# Revit family: 1. Sálvora_PDroite_FRA
name_source: partatom
category: Modelos genéricos
revit_build: Autodesk Revit LT 2017 (Build: 20160225_1515(x64)
units: mm (PartAtom-declared; Revit-internal decimal feet)

## family parameters
Anfitrión = Muro
Compartido = No
Corte con vacíos al cargar = No
Cota de conector redondo = Diámetro de uso
Puede alojar armadura = No
Punto de cálculo de habitación = No
Siempre vertical = Sí
Tipo de pieza = Normal

## types (1)
- Stonepanel®Sálvora
    Absorption = Basse absorption
    Advantages de Stonepanel = Efficacité:  L’installation des panneaux est simple et facile. Elle n’implique pas l’utilisation de machines spécifiques. La pose est dix fois plus rapide que la pose traditionnelle (20 m2 en moyenne par jour). La longévité de ce produit naturel est supérieure aux autres types de revêtement. Les déchets et les pertes dues aux coupes sont amplement diminués durant le chantier.
Sécurité: Le système de fixation breveté et homologué, en acier inoxydable, permet l’installation à plus de 2 mètres de hauteur (Avis Technique, CSTB). La base en ciment, homogène et rugueuse, garantit l’adhésion et permet d’être coupée sans décollement des pierres.
Qualité: Le contrôle de la production est effectué de façon continue par le département Innovation de CUPAGROUP. Chaque pierre naturelle est sélectionnée avec une attention particulière par les experts de CUPA STONE. Angles courts, longs, massifs, doubles, pour les fenêtres ou les dessus de mur… De nombreuses pièces spéciales sont proposées en option pour s’adapter parfaitement aux différentes configurations de chantier.
Esthétisme: Le parement en forme de « S » rend les joints invisibles et assure un aspect homogène à la surface installée. Notre gamme de parements en pierre naturelle permet de choisir parmi un large choix de finitions et de coloris. Chaque pierre est unique, ainsi chaque panneau révèle l’élégance et la noblesse de la pierre naturelle.
    Apparence = Rustique
    Autres données intéressants = STONEPANEL SKY  est utilisé pour la réalisation de revêtements de murs intérieurs ou extérieurs, pour des ouvrages de 12 m de haut au plus.
    Certificats = Avis Technique - France - En cours
    Couleur principale = Marron
    Couleur secondaire = Gris rougeâtre
    Densité apparente = 86,5 kg/m2
    Descripción = Système de panneaux de pierre naturelle prémontés et assemblés
sur une base en ciment renforcée, sur la face arrière, par une armature en fibre de verre. 
Son système de fixation unique évite tout risque de décollement. Est un ancrage spécifique pour les installations
à plus de 2 mètres de hauteur.
    Durabilité = La durabilité de l’ouvrage peut être appréciée comme équivalente à celle d’un carrelage collé en façade.
    Décalage de hauteur = 0 mm  [stored 0 ft]
    Détails de construction = Détails de:
- Mise en oeuvre avec un profilé en métal
- Mise en oeuvre de Stonepanel
- Mise en oeuvre de Stonepanel en murs intérieurs
- Mise en oeuvre de l'élément de sécurité
- Angles rentrants
- Angles sortants avec continuité de Stonepanel - éléments d'angles
- Angles sortants avec continuité de Stonepanel - angles préformés
- Angles sortants avec continuité de Stonepanel - sciage d'un panneau
- Angles sortants sans continuité de Stonepanel - cas d'un pignon isolé
- Arêtes supérieures
- Dessus d'acrotère
- Encadrement de baie
    Fabricante = Cupastone
    Finiton = Naturelle
    Form = Forme de « S »
    Format = 600 x 200
    Haut = 200 mm  [stored 0.656168 ft]
    Imagen de tipo = <Ninguno>
    Largeur = 50 mm  [stored 0.164042 ft]
    Long = 600 mm
    Matérial = Ardoise marron rougeâtre dont les nuances varient du clair au plus foncé pour doter les intérieurs contemporains d’une ambiance originale.
    Modelo = Stonepanel® Sálvora
    NBS Reference = 45-25-45/380 Natural stone panels
    Nettoyage = En général, les panneaux ne nécessitent pas d'entretien et sont autonettoyants, mais la suppression de certains types de marques peuvent nécessiter un traitement spécialisé.
Pour les salissures anormales, la surface peut être nettoyée à l'aide d'un mélange eau / détergent chaud, appliqué avec un tampon de nettoyage approprié ou une éponge.
    Omniclass = 23-15 15 15 11
    Oxydation = Non oxidé
    Poids = 9,5 kg
    Résistance = Résistance élevée
    Résistance au feu = STONEPANEL ne sont pas de nature à affecter la tenue au feu des ouvrages.
    Système d'ancrage = Bande perforée en acier inoxydable:
- Nature de l’acier : AISI 316 (1.4401) ou AISI 304 (1.4301)
- Epaisseur minimale (mm) : 0,7
- Largeur (mm) : 12 à 15
- Diamètre du trou (mm) : 6 ± 1

Chevilles:
Le choix des chevilles de fixation doit être déterminé compte tenu de l’action en dépression du vent (murs extérieurs) et de la résistance des chevilles dans le support considéré en fonction de de la nature du support. Un exemple de cheville à utiliser est TAPCO TC 6/30 x 60.
La charge admissible des chevilles est égale à 1/K fois la résistance caractéristique indiquée dans l’Agrément Technique Européen de la cheville ou :
   K = 1,75 par comparaison au vent normal
   K = 3 par comparaison au vent extrême
Les chevilles doivent être adaptées à la nature du support porteur.
    Tests effectués par Avis Technique = Avis Technique
Résistance mécanique de l'ancrage
Résistance mécanique de l'attache de sécurité
Essais de durabilité après action de l'eau
Essais de durabilité après action du gel
Essai sismique
Essai vers le feu
Résistance mécanique de l'attache de sécurité
Essais de durabilité après action de l'eau
Essais de durabilité après action du gel
Essai sismique
    Type de livraison = Les panneaux sont emballés en plastique, en paires.
    URL = http://www.cupastone.fr
    Uniclass 2 = Pr_25_71_14_56 Natural stone panels
    Uniclass 2015 = Pr_25_71_14_56 Natural stone panels
    Utilisations indiquées = Revêtements de murs intérieurs ou extérieurs, pour des ouvrages de 12 m de haut au plus.
En murs intérieurs, les supports admis sont les suivants (ils doivent avoir une épaisseur de 6 cm minimum) :
- les murs en béton,
- les panneaux préfabriqués en béton,
- les enduits à base de ciment sur murs en béton et, murs et parois
en maçonnerie.
En murs extérieurs, les supports admis sont ceux définis dans le NF DTU 52.2 P1-1-2 (P 61-204-1-1-2) « Cahier des clauses Techniques pour les murs extérieurs ».

note: [stored X ft] marks values corroborated as IEEE doubles in the binary element streams (Revit-internal decimal feet)
